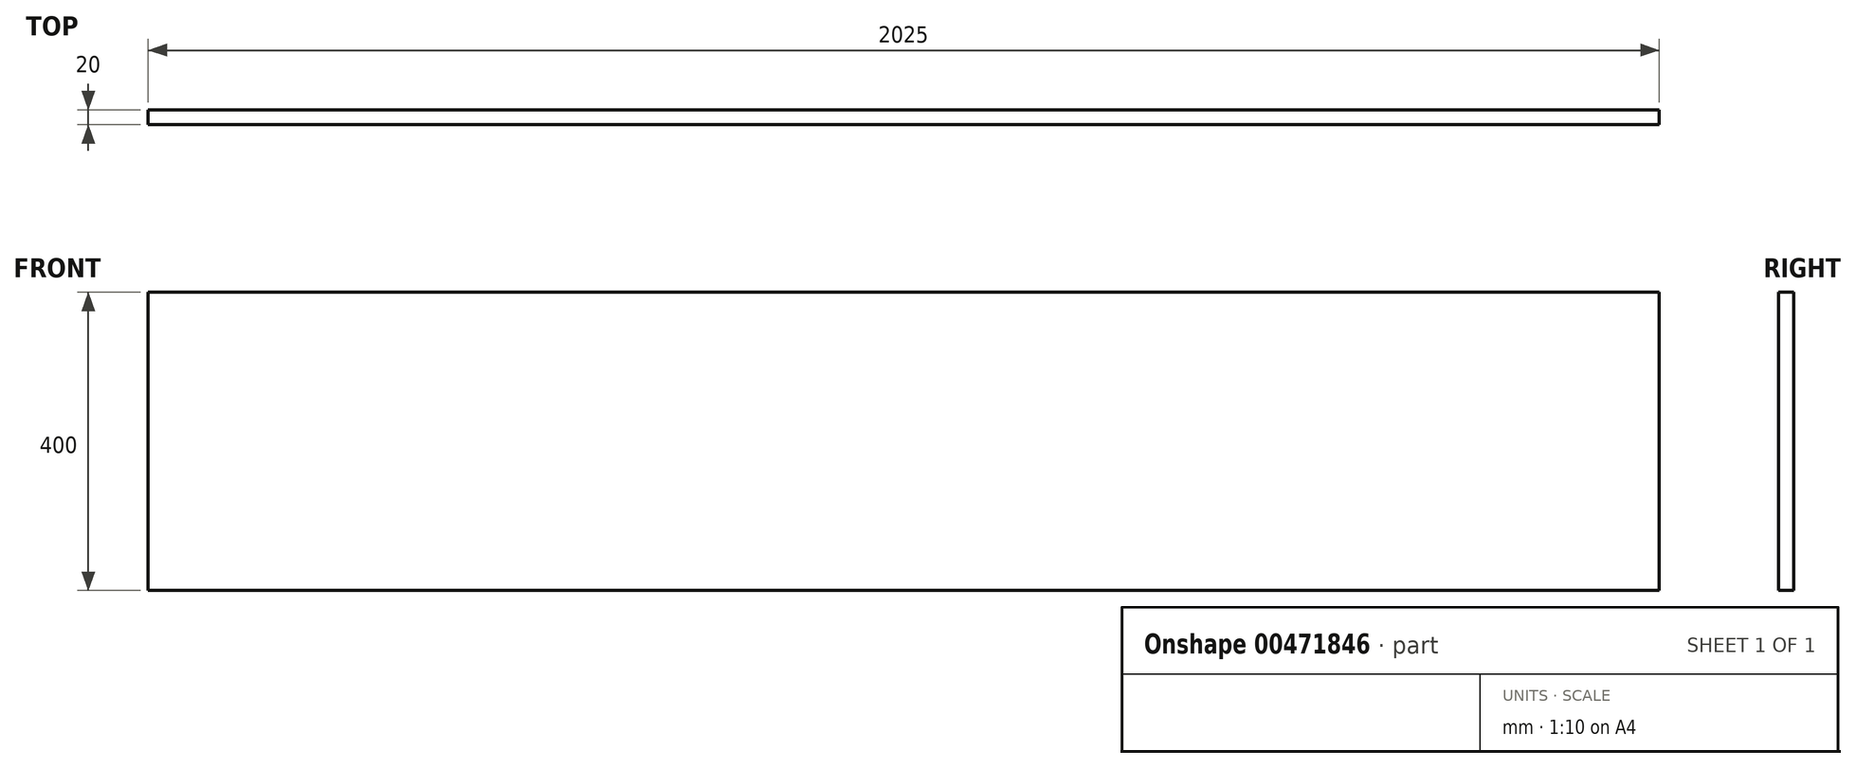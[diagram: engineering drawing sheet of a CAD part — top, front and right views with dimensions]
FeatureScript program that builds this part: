
annotation { "Feature Type Name" : "Feature", "Feature Type Description" : "" }
export const myFeature = defineFeature(function(context is Context, id is Id, definition is map)
    precondition{}
    {
        {
            var Q0;
            Q0=qCreatedBy(makeId("Front.planeOp"),FACE);
            var sketch = newSketch(context, id + "F0", { "sketchPlane" : qUnion([Q0])});
            skLineSegment(sketch, "E0.bottom", {"start": v(0, 0) * mm, "end": v(-2025, 0) * mm});
            skLineSegment(sketch, "E0.top", {"start": v(0, 400) * mm, "end": v(-2025, 400) * mm});
            skLineSegment(sketch, "E0.left", {"start": v(0, 0) * mm, "end": v(0, 400) * mm});
            skLineSegment(sketch, "E0.right", {"start": v(-2025, 0) * mm, "end": v(-2025, 400) * mm});
            skSolve(sketch);
        }
        {
            var Q0;
            Q0=makeQuery(id+"F0.imprint","IMPRINT",FACE,{"disambiguationData":[TD([[makeQuery(id+"F0.imprint","IMPRINT",EDGE,{"derivedFrom":sQuery(id+"F0.wireOp",EDGE,"E0.bottom")}),-1.0]])]});
            extrude(context, id + "F1", {"entities" : qUnion([Q0]), "depth" : 20 * mm});
        }
    });
